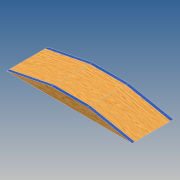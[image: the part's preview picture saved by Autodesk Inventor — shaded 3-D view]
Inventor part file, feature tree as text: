
AUTODESK INVENTOR PART (.ipt)
format: ipt  version: 2020 (Build 240168000, 168)  size: 178,688 bytes
history: native  units: mm
features: extrude x6, sketch x6
ambient origin geometry x8: Origin, YZ Plane, XZ Plane, XY Plane, X Axis, Y Axis, Z Axis, Center Point
bodies: Solid1 (feature_tree)
feature tree (12):
  extrude  "Extrusion1"  Depth=100.0mm
  extrude  "Extrusion2"  Depth=460.0mm
  extrude  "Extrusion3"  Depth=30.0mm
  extrude  "Extrusion4"  Depth=0.5mm TaperAngle=0.0deg
  extrude  "Extrusion5"  Depth=510.344311mm
  extrude  "Extrusion6"  Depth=0.5mm TaperAngle=0.0deg
  sketch  "Sketch1"  dims[d0=400.0mm d1=100.0mm]
  sketch  "Sketch2"  dims[d4=460.0mm d5=0.0mm d6=1.972222mm]
  sketch  "Sketch3"  dims[d7=29.443704mm d8=30.0mm]
  sketch  "Sketch4"  dims[d9=30.0mm d10=0.5mm d11=0.0mm]
  sketch  "Sketch5"  dims[d12=30.0mm d13=510.344311mm]
  sketch  "Sketch6"  dims[d14=30.0mm d15=0.5mm d16=0.0mm d17=30.0mm d18=30.0mm d19=0.5mm d20=0.0mm d21=460.0mm d22=0.0mm d23=460.0mm d24=0.0mm]
